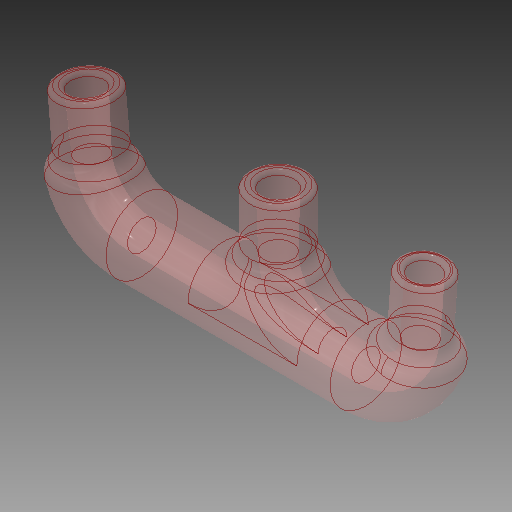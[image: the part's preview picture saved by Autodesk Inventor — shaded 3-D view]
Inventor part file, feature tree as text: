
AUTODESK INVENTOR PART (.ipt)
format: ipt  version: 2019 (Build 230136000, 136)  size: 547,840 bytes
history: native  units: mm
features: sweep x6, extrude x5, sketch x4, fillet x2
ambient origin geometry x8: Origin, YZ Plane, XZ Plane, XY Plane, X Axis, Y Axis, Z Axis, Center Point
bodies: Solid1 (feature_tree)
feature tree (17):
  sketch  "Sketch2"  dims[d2=7.0mm d3=7.0mm]
  sketch  "Sketch1"  dims[d0=7.5mm d1=7.0mm]
  sweep  "Sweep1"
  sketch  "Sketch4"  dims[d7=23.981755mm d9=1.151926mm]
  extrude  "Extrusion4"  Depth=7.0mm
  sweep  "Sweep2"
  sweep  "Sweep3"
  extrude  "Extrusion7"  Depth=0.5mm
  sweep  "Sweep8"
  extrude  "Extrusion8"  Depth=0.5mm
  fillet  "Fillet1"  Radius=9.2mm
  sweep  "Sweep7"
  extrude  "Extrusion9"  Depth=0.5mm
  sweep  "Sweep9"
  fillet  "Fillet2"  Radius=6.467703mm
  extrude  "Extrusion5"  TaperAngle=0.0deg  [1 undecoded]
  sketch  "Sketch5"  dims[d10=7.5mm d11=2.4824mm d12=18.5mm d13=0.759218mm d14=5.0mm d15=9.2mm d16=6.1mm d17=3.7mm d18=0.959508mm d19=6.467703mm d20=0.0mm d21=0.0mm d22=0.0mm d23=0.0mm d26=0.0mm d27=0.0mm d32=9.2mm d33=9.2mm d34=20.0mm d35=0.0mm d38=4.6mm d41=3.7mm d44=20.0mm d45=0.0mm d46=0.0mm d47=0.0mm d51=2.0mm d53=7.17mm d54=20.0mm d55=0.0mm d56=0.0mm d57=0.0mm d58=20.0mm d59=0.296706mm d60=20.0mm d61=0.296706mm d62=0.0mm d63=0.0mm d64=1.5mm d65=0.5mm]
note: 1 required parameter value undecoded (feature->parameter linkage not recoverable at this tier; creation-order binding heuristic only, values carry confidence <= 0.55)
